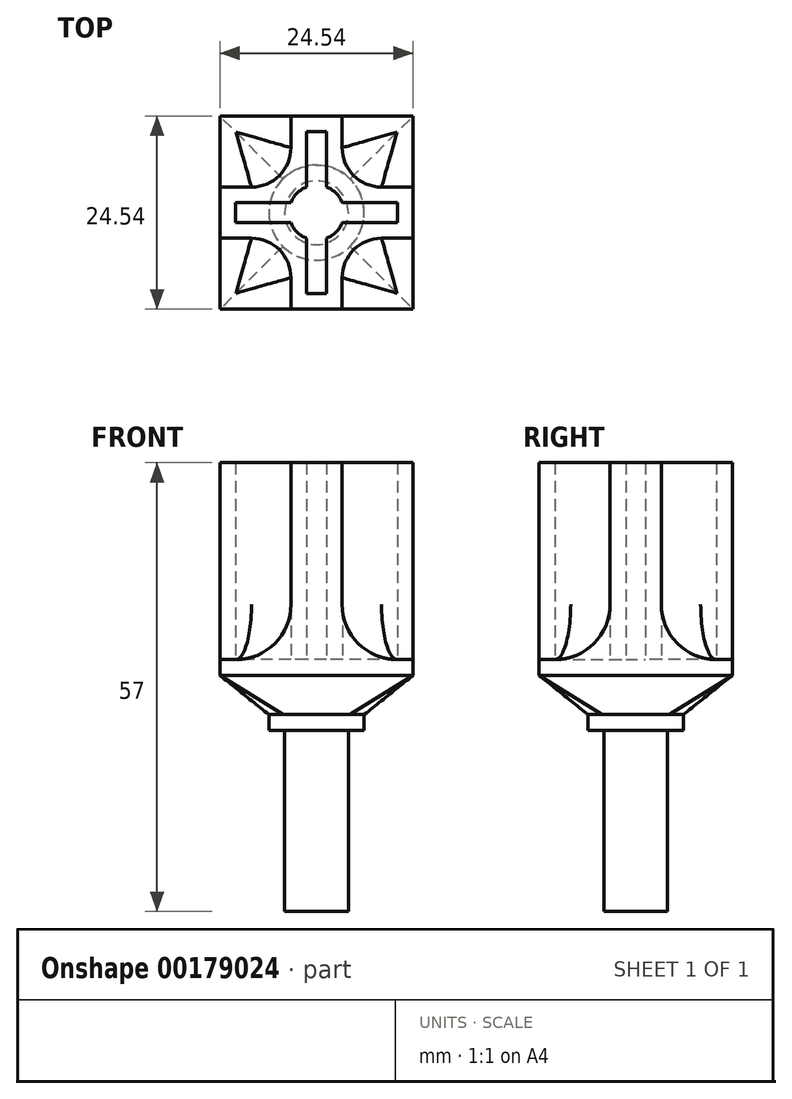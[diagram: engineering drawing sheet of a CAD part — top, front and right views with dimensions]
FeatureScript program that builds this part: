
annotation { "Feature Type Name" : "Feature", "Feature Type Description" : "" }
export const myFeature = defineFeature(function(context is Context, id is Id, definition is map)
    precondition{}
    {
        {
            var Q0;
            Q0=qCreatedBy(makeId("Top.planeOp"),FACE);
            var sketch = newSketch(context, id + "F0", { "sketchPlane" : qUnion([Q0])});
            skCircle(sketch, "E0", {"center": v(0, 0) * mm, "radius": 3.5 * mm});
            skLineSegment(sketch, "E1", {"start": v(-3.27, 1.25) * mm, "end": v(-10.27, 1.25) * mm});
            skLineSegment(sketch, "E2", {"start": v(-10.27, 1.25) * mm, "end": v(-10.27, -1.25) * mm});
            skLineSegment(sketch, "E3", {"start": v(-10.27, -1.25) * mm, "end": v(-3.27, -1.25) * mm});
            skCircle(sketch, "E4", {"center": v(0, 0) * mm, "radius": 4.5 * mm});
            skLineSegment(sketch, "E5", {"start": v(-1.3, -3.25) * mm, "end": v(-12.27, -3.25) * mm});
            skLineSegment(sketch, "E6", {"start": v(-12.27, -3.25) * mm, "end": v(-12.27, 3.25) * mm});
            skLineSegment(sketch, "E7", {"start": v(-12.27, 3.25) * mm, "end": v(-1.3, 3.25) * mm});
            skLineSegment(sketch, "E8.1.0", {"start": v(-3.25, -12.27) * mm, "end": v(-3.25, -1.3) * mm});
            skLineSegment(sketch, "E8.1.1", {"start": v(-1.25, -3.27) * mm, "end": v(-1.25, -10.27) * mm});
            skLineSegment(sketch, "E8.1.2", {"start": v(-1.25, -10.27) * mm, "end": v(1.25, -10.27) * mm});
            skLineSegment(sketch, "E8.1.3", {"start": v(1.25, -10.27) * mm, "end": v(1.25, -3.27) * mm});
            skLineSegment(sketch, "E8.1.4", {"start": v(3.25, -1.3) * mm, "end": v(3.25, -12.27) * mm});
            skLineSegment(sketch, "E8.1.5", {"start": v(3.25, -12.27) * mm, "end": v(-3.25, -12.27) * mm});
            skLineSegment(sketch, "E8.2.0", {"start": v(12.27, -3.25) * mm, "end": v(1.3, -3.25) * mm});
            skLineSegment(sketch, "E8.2.1", {"start": v(3.27, -1.25) * mm, "end": v(10.27, -1.25) * mm});
            skLineSegment(sketch, "E8.2.2", {"start": v(10.27, -1.25) * mm, "end": v(10.27, 1.25) * mm});
            skLineSegment(sketch, "E8.2.3", {"start": v(10.27, 1.25) * mm, "end": v(3.27, 1.25) * mm});
            skLineSegment(sketch, "E8.2.4", {"start": v(1.3, 3.25) * mm, "end": v(12.27, 3.25) * mm});
            skLineSegment(sketch, "E8.2.5", {"start": v(12.27, 3.25) * mm, "end": v(12.27, -3.25) * mm});
            skLineSegment(sketch, "E8.3.0", {"start": v(3.25, 12.27) * mm, "end": v(3.25, 1.3) * mm});
            skLineSegment(sketch, "E8.3.1", {"start": v(1.25, 3.27) * mm, "end": v(1.25, 10.27) * mm});
            skLineSegment(sketch, "E8.3.2", {"start": v(1.25, 10.27) * mm, "end": v(-1.25, 10.27) * mm});
            skLineSegment(sketch, "E8.3.3", {"start": v(-1.25, 10.27) * mm, "end": v(-1.25, 3.27) * mm});
            skLineSegment(sketch, "E8.3.4", {"start": v(-3.25, 1.3) * mm, "end": v(-3.25, 12.27) * mm});
            skLineSegment(sketch, "E8.3.5", {"start": v(-3.25, 12.27) * mm, "end": v(3.25, 12.27) * mm});
            skSolve(sketch);
        }
        {
            var Q0;
            Q0=qSketchRegion(id+"F0",true);
            var Q1;
            {var subQ0=sQuery(id+"F0.wireOp",EDGE,"E5");var subQ1=sQuery(id+"F0.wireOp",EDGE,"E0");var subQ2=makeQuery(id+"F0.imprint","INTERSECT",VERTEX,{"derivedFrom":[subQ1,subQ0]});Q1=makeQuery(id+"F0.imprint","IMPRINT",FACE,{"disambiguationData":[TD([[makeQuery(id+"F0.imprint","IMPRINT",EDGE,{"disambiguationData":[TD([[subQ2,1.0]])],"derivedFrom":subQ1}),-1.0]])]});}
            var Q2;
            {var subQ0=sQuery(id+"F0.wireOp",EDGE,"E3");var subQ1=sQuery(id+"F0.wireOp",EDGE,"E0");var subQ2=makeQuery(id+"F0.imprint","INTERSECT",VERTEX,{"derivedFrom":[subQ1,subQ0]});Q2=makeQuery(id+"F0.imprint","IMPRINT",FACE,{"disambiguationData":[TD([[makeQuery(id+"F0.imprint","IMPRINT",EDGE,{"disambiguationData":[TD([[subQ2,-1.0]])],"derivedFrom":subQ1}),-1.0]])]});}
            var Q3;
            {var subQ0=sQuery(id+"F0.wireOp",EDGE,"E5");var subQ1=sQuery(id+"F0.wireOp",EDGE,"E0");var subQ2=makeQuery(id+"F0.imprint","INTERSECT",VERTEX,{"derivedFrom":[subQ1,subQ0]});Q3=makeQuery(id+"F0.imprint","IMPRINT",FACE,{"disambiguationData":[TD([[makeQuery(id+"F0.imprint","IMPRINT",EDGE,{"disambiguationData":[TD([[subQ2,-1.0]])],"derivedFrom":subQ1}),-1.0]])]});}
            var Q4;
            {var subQ0=sQuery(id+"F0.wireOp",EDGE,"E1");var subQ1=sQuery(id+"F0.wireOp",EDGE,"E0");var subQ2=makeQuery(id+"F0.imprint","INTERSECT",VERTEX,{"derivedFrom":[subQ1,subQ0]});Q4=makeQuery(id+"F0.imprint","IMPRINT",FACE,{"disambiguationData":[TD([[makeQuery(id+"F0.imprint","IMPRINT",EDGE,{"disambiguationData":[TD([[subQ2,1.0]])],"derivedFrom":subQ1}),-1.0]])]});}
            var Q5;
            {var subQ0=sQuery(id+"F0.wireOp",EDGE,"E7");var subQ1=sQuery(id+"F0.wireOp",EDGE,"E0");var subQ2=makeQuery(id+"F0.imprint","INTERSECT",VERTEX,{"derivedFrom":[subQ1,subQ0]});Q5=makeQuery(id+"F0.imprint","IMPRINT",FACE,{"disambiguationData":[TD([[makeQuery(id+"F0.imprint","IMPRINT",EDGE,{"disambiguationData":[TD([[subQ2,-1.0]])],"derivedFrom":subQ1}),-1.0]])]});}
            var Q6;
            {var subQ0=sQuery(id+"F0.wireOp",EDGE,"E7");var subQ1=sQuery(id+"F0.wireOp",EDGE,"E0");var subQ2=makeQuery(id+"F0.imprint","INTERSECT",VERTEX,{"derivedFrom":[subQ1,subQ0]});Q6=makeQuery(id+"F0.imprint","IMPRINT",FACE,{"disambiguationData":[TD([[makeQuery(id+"F0.imprint","IMPRINT",EDGE,{"disambiguationData":[TD([[subQ2,1.0]])],"derivedFrom":subQ1}),-1.0]])]});}
            var Q7;
            {var subQ0=sQuery(id+"F0.wireOp",EDGE,"E8.2.4");var subQ1=sQuery(id+"F0.wireOp",EDGE,"E0");var subQ2=makeQuery(id+"F0.imprint","INTERSECT",VERTEX,{"derivedFrom":[subQ1,subQ0]});Q7=makeQuery(id+"F0.imprint","IMPRINT",FACE,{"disambiguationData":[TD([[makeQuery(id+"F0.imprint","IMPRINT",EDGE,{"disambiguationData":[TD([[subQ2,-1.0]])],"derivedFrom":subQ1}),-1.0]])]});}
            var Q8;
            {var subQ0=sQuery(id+"F0.wireOp",EDGE,"E8.2.4");var subQ1=sQuery(id+"F0.wireOp",EDGE,"E0");var subQ2=makeQuery(id+"F0.imprint","INTERSECT",VERTEX,{"derivedFrom":[subQ1,subQ0]});Q8=makeQuery(id+"F0.imprint","IMPRINT",FACE,{"disambiguationData":[TD([[makeQuery(id+"F0.imprint","IMPRINT",EDGE,{"disambiguationData":[TD([[subQ2,1.0]])],"derivedFrom":subQ1}),-1.0]])]});}
            var Q9;
            {var subQ0=sQuery(id+"F0.wireOp",EDGE,"E8.2.3");var subQ1=sQuery(id+"F0.wireOp",EDGE,"E0");var subQ2=makeQuery(id+"F0.imprint","INTERSECT",VERTEX,{"derivedFrom":[subQ1,subQ0]});Q9=makeQuery(id+"F0.imprint","IMPRINT",FACE,{"disambiguationData":[TD([[makeQuery(id+"F0.imprint","IMPRINT",EDGE,{"disambiguationData":[TD([[subQ2,-1.0]])],"derivedFrom":subQ1}),-1.0]])]});}
            var Q10;
            {var subQ0=sQuery(id+"F0.wireOp",EDGE,"E8.1.4");var subQ1=sQuery(id+"F0.wireOp",EDGE,"E0");var subQ2=makeQuery(id+"F0.imprint","INTERSECT",VERTEX,{"derivedFrom":[subQ1,subQ0]});Q10=makeQuery(id+"F0.imprint","IMPRINT",FACE,{"disambiguationData":[TD([[makeQuery(id+"F0.imprint","IMPRINT",EDGE,{"disambiguationData":[TD([[subQ2,1.0]])],"derivedFrom":subQ1}),-1.0]])]});}
            var Q11;
            {var subQ0=sQuery(id+"F0.wireOp",EDGE,"E8.1.3");var subQ1=sQuery(id+"F0.wireOp",EDGE,"E0");var subQ2=makeQuery(id+"F0.imprint","INTERSECT",VERTEX,{"derivedFrom":[subQ1,subQ0]});Q11=makeQuery(id+"F0.imprint","IMPRINT",FACE,{"disambiguationData":[TD([[makeQuery(id+"F0.imprint","IMPRINT",EDGE,{"disambiguationData":[TD([[subQ2,-1.0]])],"derivedFrom":subQ1}),-1.0]])]});}
            var Q12;
            {var subQ0=sQuery(id+"F0.wireOp",EDGE,"E8.1.4");var subQ1=sQuery(id+"F0.wireOp",EDGE,"E0");var subQ2=makeQuery(id+"F0.imprint","INTERSECT",VERTEX,{"derivedFrom":[subQ1,subQ0]});Q12=makeQuery(id+"F0.imprint","IMPRINT",FACE,{"disambiguationData":[TD([[makeQuery(id+"F0.imprint","IMPRINT",EDGE,{"disambiguationData":[TD([[subQ2,-1.0]])],"derivedFrom":subQ1}),-1.0]])]});}
            extrude(context, id + "F1", {"entities" : qUnion([Q0, Q1, Q2, Q3, Q4, Q5, Q6, Q7, Q8, Q9, Q10, Q11, Q12]), "depth" : 25 * mm});
        }
        {
            var Q0;
            Q0=makeQuery(id+"F1.opExtrude","CAP_FACE",FACE,{"disambiguationData":[OSD([sQuery(id+"F0.wireOp",EDGE,"E0"),sQuery(id+"F0.wireOp",EDGE,"E1"),sQuery(id+"F0.wireOp",EDGE,"E2"),sQuery(id+"F0.wireOp",EDGE,"E3"),sQuery(id+"F0.wireOp",EDGE,"E5"),sQuery(id+"F0.wireOp",EDGE,"E6"),sQuery(id+"F0.wireOp",EDGE,"E7"),sQuery(id+"F0.wireOp",EDGE,"E8.1.0"),sQuery(id+"F0.wireOp",EDGE,"E8.1.1"),sQuery(id+"F0.wireOp",EDGE,"E8.1.2"),sQuery(id+"F0.wireOp",EDGE,"E8.1.3"),sQuery(id+"F0.wireOp",EDGE,"E8.1.4"),sQuery(id+"F0.wireOp",EDGE,"E8.1.5"),sQuery(id+"F0.wireOp",EDGE,"E8.2.0"),sQuery(id+"F0.wireOp",EDGE,"E8.2.1"),sQuery(id+"F0.wireOp",EDGE,"E8.2.2"),sQuery(id+"F0.wireOp",EDGE,"E8.2.3"),sQuery(id+"F0.wireOp",EDGE,"E8.2.4"),sQuery(id+"F0.wireOp",EDGE,"E8.2.5"),sQuery(id+"F0.wireOp",EDGE,"E8.3.0"),sQuery(id+"F0.wireOp",EDGE,"E8.3.1"),sQuery(id+"F0.wireOp",EDGE,"E8.3.2"),sQuery(id+"F0.wireOp",EDGE,"E8.3.3"),sQuery(id+"F0.wireOp",EDGE,"E8.3.4"),sQuery(id+"F0.wireOp",EDGE,"E8.3.5")])],"isStart":true});
            var sketch = newSketch(context, id + "F2", { "sketchPlane" : qUnion([Q0])});
            skLineSegment(sketch, "E9.bottom", {"start": v(-12.27, 12.27) * mm, "end": v(12.27, 12.27) * mm});
            skLineSegment(sketch, "E9.top", {"start": v(-12.27, -12.27) * mm, "end": v(12.27, -12.27) * mm});
            skLineSegment(sketch, "E9.left", {"start": v(-12.27, 12.27) * mm, "end": v(-12.27, -12.27) * mm});
            skLineSegment(sketch, "E9.right", {"start": v(12.27, 12.27) * mm, "end": v(12.27, -12.27) * mm});
            skSolve(sketch);
        }
        {
            var Q0;
            Q0=qSketchRegion(id+"F2",true);
            extrude(context, id + "F3", {"entities" : qUnion([Q0]), "operationType" : NewBodyOperationType.ADD, "depth" : 2 * mm});
        }
        {
            var Q0;
            Q0=makeQuery(id+"F3.opExtrude","CAP_FACE",FACE,{"disambiguationData":[OSD([sQuery(id+"F2.wireOp",EDGE,"E9.bottom"),sQuery(id+"F2.wireOp",EDGE,"E9.top"),sQuery(id+"F2.wireOp",EDGE,"E9.left"),sQuery(id+"F2.wireOp",EDGE,"E9.right")])],"isStart":false});
            cPlane(context, id + "F4", {"entities" : qUnion([Q0]), "cplaneType" : CPlaneType.OFFSET, "offset" : 5 * mm, "width" : 150 * mm, "height" : 150 * mm});
        }
        {
            var Q0;
            Q0=qCreatedBy(id+"F4.planeOp",FACE);
            var sketch = newSketch(context, id + "F5", { "sketchPlane" : qUnion([Q0])});
            skCircle(sketch, "E10", {"center": v(0, 0) * mm, "radius": 4.05 * mm});
            skCircle(sketch, "E11", {"center": v(0, 0) * mm, "radius": 6.05 * mm});
            skSolve(sketch);
        }
        {
            var Q0;
            Q0=makeQuery(id+"F5.imprint","IMPRINT",FACE,{"disambiguationData":[TD([[makeQuery(id+"F5.imprint","IMPRINT",EDGE,{"derivedFrom":sQuery(id+"F5.wireOp",EDGE,"E10")}),1.0]])]});
            extrude(context, id + "F6", {"entities" : qUnion([Q0]), "depth" : 25 * mm});
        }
        {
            var Q0;
            Q0=makeQuery(id+"F5.imprint","IMPRINT",FACE,{"disambiguationData":[TD([[makeQuery(id+"F5.imprint","IMPRINT",EDGE,{"derivedFrom":sQuery(id+"F5.wireOp",EDGE,"E10")}),-1.0]])]});
            extrude(context, id + "F7", {"entities" : qUnion([Q0]), "operationType" : NewBodyOperationType.ADD, "depth" : 2 * mm});
        }
        {
            var Q1;
            {var subQ0=sQuery(id+"F5.wireOp",EDGE,"E10");Q1=makeQuery(id+"F7.boolean.opBoolean","MERGE",FACE,{"derivedFrom":[makeQuery(id+"F6.opExtrude","CAP_FACE",FACE,{"disambiguationData":[OSD([subQ0])],"isStart":true}),makeQuery(id+"F7.opExtrude","CAP_FACE",FACE,{"disambiguationData":[OSD([subQ0,sQuery(id+"F5.wireOp",EDGE,"E11")])],"isStart":true})]});}
            var Q2;
            Q2=makeQuery(id+"F3.opExtrude","CAP_FACE",FACE,{"disambiguationData":[OSD([sQuery(id+"F2.wireOp",EDGE,"E9.bottom"),sQuery(id+"F2.wireOp",EDGE,"E9.top"),sQuery(id+"F2.wireOp",EDGE,"E9.left"),sQuery(id+"F2.wireOp",EDGE,"E9.right")])],"isStart":false});
            loft(context, id + "F8", {"operationType" : NewBodyOperationType.ADD, "sheetProfilesArray" : [{ "sheetProfileEntities" : qUnion([Q1]) }, { "sheetProfileEntities" : qUnion([Q2]) }]});
        }
        {
            var Q0;
            Q0=makeQuery(id+"F1.opExtrude","CAP_EDGE",EDGE,{"disambiguationData":[OSD([sQuery(id+"F0.wireOp",EDGE,"E7")])],"isStart":true});
            var Q1;
            Q1=makeQuery(id+"F1.opExtrude","CAP_EDGE",EDGE,{"disambiguationData":[OSD([sQuery(id+"F0.wireOp",EDGE,"E8.3.4")])],"isStart":true});
            var Q2;
            Q2=makeQuery(id+"F1.opExtrude","CAP_EDGE",EDGE,{"disambiguationData":[OSD([sQuery(id+"F0.wireOp",EDGE,"E8.3.0")])],"isStart":true});
            var Q3;
            Q3=makeQuery(id+"F1.opExtrude","CAP_EDGE",EDGE,{"disambiguationData":[OSD([sQuery(id+"F0.wireOp",EDGE,"E8.2.4")])],"isStart":true});
            var Q4;
            Q4=makeQuery(id+"F1.opExtrude","CAP_EDGE",EDGE,{"disambiguationData":[OSD([sQuery(id+"F0.wireOp",EDGE,"E5")])],"isStart":true});
            var Q5;
            Q5=makeQuery(id+"F1.opExtrude","CAP_EDGE",EDGE,{"disambiguationData":[OSD([sQuery(id+"F0.wireOp",EDGE,"E8.1.0")])],"isStart":true});
            var Q6;
            Q6=makeQuery(id+"F1.opExtrude","CAP_EDGE",EDGE,{"disambiguationData":[OSD([sQuery(id+"F0.wireOp",EDGE,"E8.1.4")])],"isStart":true});
            var Q7;
            Q7=makeQuery(id+"F1.opExtrude","CAP_EDGE",EDGE,{"disambiguationData":[OSD([sQuery(id+"F0.wireOp",EDGE,"E8.2.0")])],"isStart":true});
            fillet(context, id + "F9", {"entities" : qUnion([Q0, Q1, Q2, Q3, Q4, Q5, Q6, Q7]), "radius" : 7 * mm, "tangentPropagation" : true, "allowEdgeOverflow" : false});
        }
        {
            var Q0;
            Q0=makeQuery(id+"F9.opFillet","BLEND_EDGE",EDGE,{"blendedFrom":[makeQuery(id+"F1.opExtrude","CAP_EDGE",EDGE,{"disambiguationData":[OSD([sQuery(id+"F0.wireOp",EDGE,"E5")])],"isStart":true}),makeQuery(id+"F1.opExtrude","CAP_EDGE",EDGE,{"disambiguationData":[OSD([sQuery(id+"F0.wireOp",EDGE,"E8.1.0")])],"isStart":true})],"blendedInto":[]});
            var Q1;
            Q1=makeQuery(id+"F9.opFillet","BLEND_EDGE",EDGE,{"blendedFrom":[makeQuery(id+"F1.opExtrude","CAP_EDGE",EDGE,{"disambiguationData":[OSD([sQuery(id+"F0.wireOp",EDGE,"E7")])],"isStart":true}),makeQuery(id+"F1.opExtrude","CAP_EDGE",EDGE,{"disambiguationData":[OSD([sQuery(id+"F0.wireOp",EDGE,"E8.3.4")])],"isStart":true})],"blendedInto":[]});
            var Q2;
            Q2=makeQuery(id+"F9.opFillet","BLEND_EDGE",EDGE,{"blendedFrom":[makeQuery(id+"F1.opExtrude","CAP_EDGE",EDGE,{"disambiguationData":[OSD([sQuery(id+"F0.wireOp",EDGE,"E8.2.4")])],"isStart":true}),makeQuery(id+"F1.opExtrude","CAP_EDGE",EDGE,{"disambiguationData":[OSD([sQuery(id+"F0.wireOp",EDGE,"E8.3.0")])],"isStart":true})],"blendedInto":[]});
            var Q3;
            Q3=makeQuery(id+"F9.opFillet","BLEND_EDGE",EDGE,{"blendedFrom":[makeQuery(id+"F1.opExtrude","CAP_EDGE",EDGE,{"disambiguationData":[OSD([sQuery(id+"F0.wireOp",EDGE,"E8.1.4")])],"isStart":true}),makeQuery(id+"F1.opExtrude","CAP_EDGE",EDGE,{"disambiguationData":[OSD([sQuery(id+"F0.wireOp",EDGE,"E8.2.0")])],"isStart":true})],"blendedInto":[]});
            fillet(context, id + "F10", {"entities" : qUnion([Q0, Q1, Q2, Q3]), "radius" : 5 * mm, "tangentPropagation" : true, "allowEdgeOverflow" : false});
        }
    });
